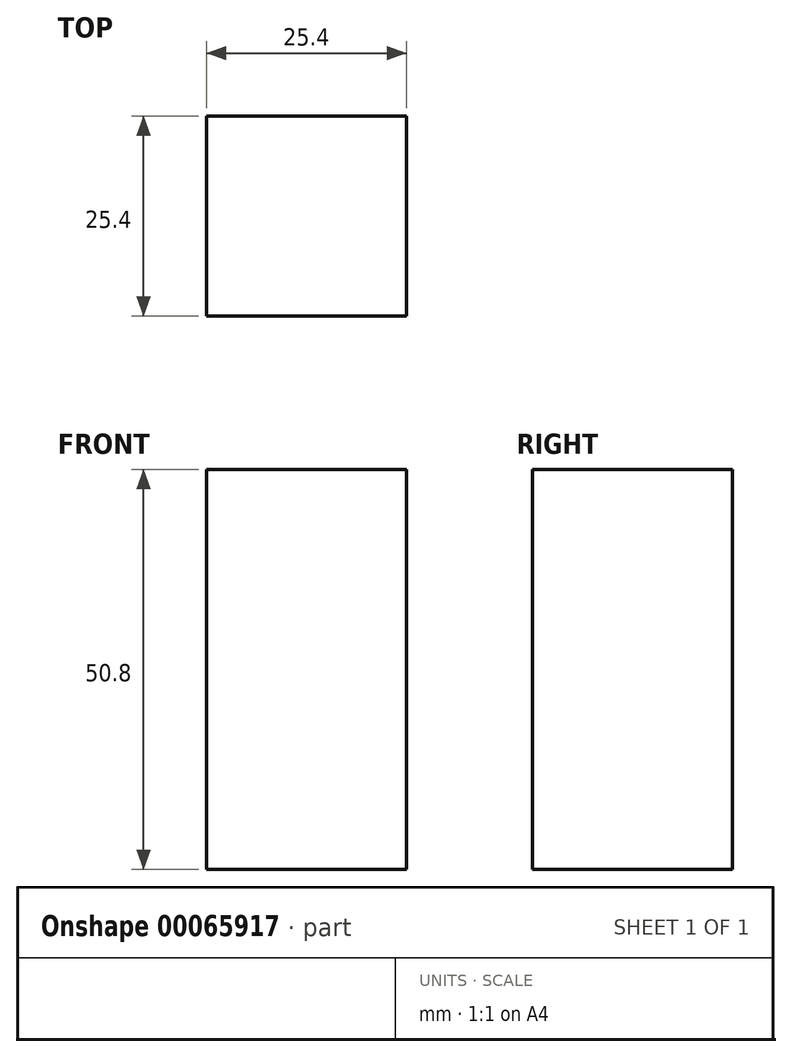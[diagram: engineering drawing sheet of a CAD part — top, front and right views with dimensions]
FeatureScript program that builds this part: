
annotation { "Feature Type Name" : "Feature", "Feature Type Description" : "" }
export const myFeature = defineFeature(function(context is Context, id is Id, definition is map)
    precondition{}
    {
        {
            var Q0;
            Q0=qCreatedBy(makeId("Front.planeOp"),FACE);
            var sketch = newSketch(context, id + "F0", { "sketchPlane" : qUnion([Q0])});
            skLineSegment(sketch, "E0.bottom", {"start": v(0, 0) * mm, "end": v(25.4, 0) * mm});
            skLineSegment(sketch, "E0.top", {"start": v(0, -25.4) * mm, "end": v(25.4, -25.4) * mm});
            skLineSegment(sketch, "E0.left", {"start": v(0, 0) * mm, "end": v(0, -25.4) * mm});
            skLineSegment(sketch, "E0.right", {"start": v(25.4, 0) * mm, "end": v(25.4, -25.4) * mm});
            skSolve(sketch);
        }
        {
            var Q0;
            Q0 = qSketchRegion(id + "F0", true);
            extrude(context, id + "F1", {"entities" : qUnion([Q0]), "depth" : 25.4 * mm});
        }
        {
            var Q0;
            Q0=makeQuery(id+"F1.opExtrude","SWEPT_FACE",FACE,{"disambiguationData":[OSD([sQuery(id+"F0.wireOp",EDGE,"E0.bottom")])]});
            var sketch = newSketch(context, id + "F2", { "sketchPlane" : qUnion([Q0])});
            skLineSegment(sketch, "E1.bottom", {"start": v(0, 0) * mm, "end": v(25.4, 0) * mm});
            skLineSegment(sketch, "E1.top", {"start": v(0, -25.4) * mm, "end": v(25.4, -25.4) * mm});
            skLineSegment(sketch, "E1.left", {"start": v(0, 0) * mm, "end": v(0, -25.4) * mm});
            skLineSegment(sketch, "E1.right", {"start": v(25.4, 0) * mm, "end": v(25.4, -25.4) * mm});
            skSolve(sketch);
        }
        {
            var Q0;
            Q0 = qSketchRegion(id + "F2", true);
            extrude(context, id + "F3", {"entities" : qUnion([Q0]), "operationType" : NewBodyOperationType.ADD, "depth" : 25.4 * mm});
        }
    });
